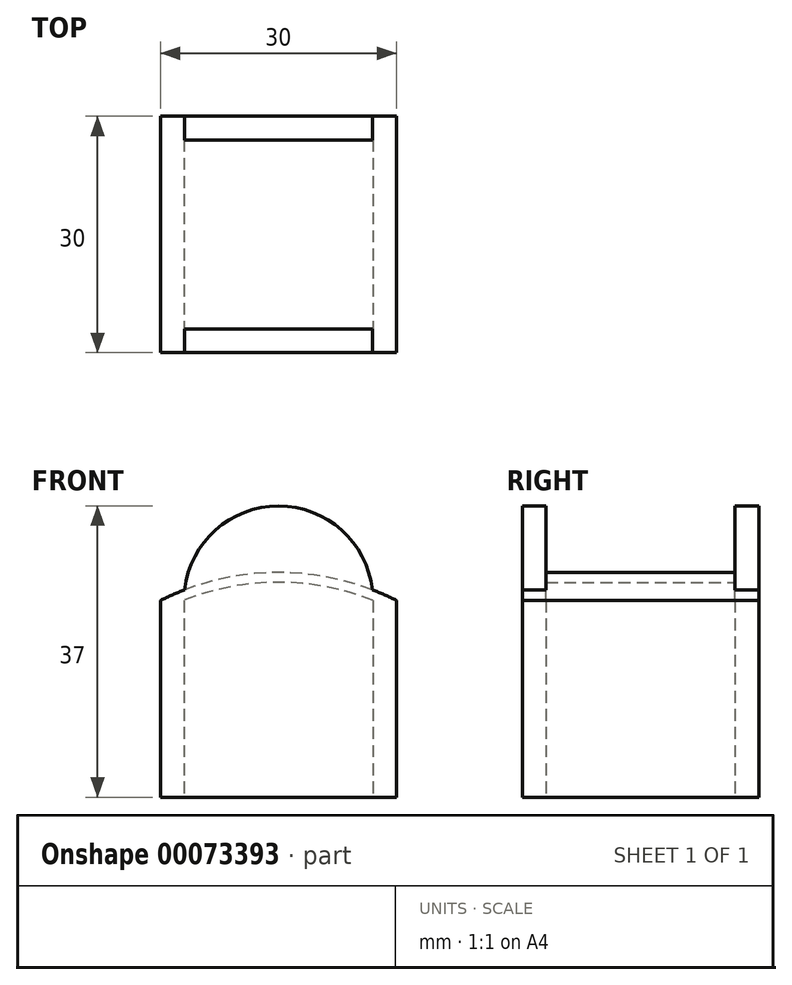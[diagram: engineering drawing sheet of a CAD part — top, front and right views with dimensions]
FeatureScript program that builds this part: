
annotation { "Feature Type Name" : "Feature", "Feature Type Description" : "" }
export const myFeature = defineFeature(function(context is Context, id is Id, definition is map)
    precondition{}
    {
        {
            var Q0;
            Q0=qCreatedBy(makeId("Top.planeOp"),FACE);
            var sketch = newSketch(context, id + "F0", { "sketchPlane" : qUnion([Q0])});
            skLineSegment(sketch, "E0.rect.bottom", {"start": v(15, 15) * mm, "end": v(-15, 15) * mm});
            skLineSegment(sketch, "E0.rect.top", {"start": v(15, -15) * mm, "end": v(-15, -15) * mm});
            skLineSegment(sketch, "E0.rect.left", {"start": v(15, 15) * mm, "end": v(15, -15) * mm});
            skLineSegment(sketch, "E0.rect.right", {"start": v(-15, 15) * mm, "end": v(-15, -15) * mm});
            skPoint(sketch, "E0.rect.middle", {"position": v(0, 0) * mm});
            skLineSegment(sketch, "E1.0", {"start": v(12, 12) * mm, "end": v(-12, 12) * mm});
            skLineSegment(sketch, "E1.1", {"start": v(12, 12) * mm, "end": v(12, -12) * mm});
            skLineSegment(sketch, "E1.2", {"start": v(12, -12) * mm, "end": v(-12, -12) * mm});
            skLineSegment(sketch, "E1.3", {"start": v(-12, 12) * mm, "end": v(-12, -12) * mm});
            skSolve(sketch);
        }
        {
            var Q0;
            Q0 = qSketchRegion(id + "F0", true);
            extrude(context, id + "F1", {"entities" : qUnion([Q0]), "depth" : 25 * mm});
        }
        {
            var Q0;
            Q0=qCreatedBy(makeId("Front.planeOp"),FACE);
            var sketch = newSketch(context, id + "F2", { "sketchPlane" : qUnion([Q0])});
            skArc(sketch, "E2", {"start": v(15, 25) * mm, "mid": v(0, 28.54) * mm, "end": v(-15, 25) * mm});
            skArc(sketch, "E3.0", {"start": v(12, 25) * mm, "mid": v(0, 27.31) * mm, "end": v(-12, 25) * mm});
            skLineSegment(sketch, "E4", {"start": v(-15, 25) * mm, "end": v(-12, 25) * mm});
            skLineSegment(sketch, "E5", {"start": v(12, 25) * mm, "end": v(15, 25) * mm});
            skLineSegment(sketch, "E6", {"start": v(0, 25) * mm, "end": v(0, -5) * mm, "construction": true});
            skLineSegment(sketch, "E7", {"start": v(-12, 25) * mm, "end": v(12, 25) * mm, "construction": true});
            skSolve(sketch);
        }
        {
            var Q0;
            Q0=makeQuery(id+"F2.imprint","IMPRINT",FACE,{"disambiguationData":[TD([[makeQuery(id+"F2.imprint","IMPRINT",EDGE,{"derivedFrom":sQuery(id+"F2.wireOp",EDGE,"E2")}),1.0]])]});
            var Q1;
            Q1=makeQuery(id+"F1.opExtrude","SWEPT_FACE",FACE,{"disambiguationData":[OSD([sQuery(id+"F0.wireOp",EDGE,"E0.rect.top")])]});
            var Q2;
            Q2=makeQuery(id+"F1.opExtrude","SWEPT_FACE",FACE,{"disambiguationData":[OSD([sQuery(id+"F0.wireOp",EDGE,"E0.rect.bottom")])]});
            extrude(context, id + "F3", {"entities" : qUnion([Q0]), "operationType" : NewBodyOperationType.ADD, "endBound" : BoundingType.UP_TO_SURFACE, "endBoundEntityFace" : qUnion([Q1]), "depth" : 25 * mm, "hasSecondDirection" : true, "secondDirectionBound" : SecondDirectionBoundingType.UP_TO_SURFACE, "secondDirectionOppositeDirection" : true, "secondDirectionBoundEntityFace" : qUnion([Q2]), "secondDirectionDepth" : 25 * mm});
        }
        {
            var Q0;
            Q0=makeQuery(id+"F3.boolean.opBoolean","MERGE",FACE,{"derivedFrom":[makeQuery(id+"F1.opExtrude","SWEPT_FACE",FACE,{"disambiguationData":[OSD([sQuery(id+"F0.wireOp",EDGE,"E0.rect.bottom")])]}),makeQuery(id+"F3.opExtrude","CAP_FACE",FACE,{"disambiguationData":[OSD([sQuery(id+"F2.wireOp",EDGE,"E2"),sQuery(id+"F2.wireOp",EDGE,"E3.0"),sQuery(id+"F2.wireOp",EDGE,"E4"),sQuery(id+"F2.wireOp",EDGE,"E5")])],"isStart":true})]});
            var sketch = newSketch(context, id + "F4", { "sketchPlane" : qUnion([Q0])});
            skArc(sketch, "E8", {"start": v(12, 25) * mm, "mid": v(0, 37) * mm, "end": v(-12, 25) * mm});
            skLineSegment(sketch, "E9", {"start": v(-12, 25) * mm, "end": v(12, 25) * mm});
            skSolve(sketch);
        }
        {
            var Q0;
            Q0 = qSketchRegion(id + "F4", true);
            var Q1;
            Q1=makeQuery(id+"F1.opExtrude","SWEPT_FACE",FACE,{"disambiguationData":[OSD([sQuery(id+"F0.wireOp",EDGE,"E1.0")])]});
            extrude(context, id + "F5", {"entities" : qUnion([Q0]), "operationType" : NewBodyOperationType.ADD, "endBound" : BoundingType.UP_TO_SURFACE, "oppositeDirection" : true, "endBoundEntityFace" : qUnion([Q1]), "depth" : 25 * mm});
        }
        {
            var Q0;
            Q0=makeQuery(id+"F3.boolean.opBoolean","MERGE",FACE,{"derivedFrom":[makeQuery(id+"F1.opExtrude","SWEPT_FACE",FACE,{"disambiguationData":[OSD([sQuery(id+"F0.wireOp",EDGE,"E0.rect.top")])]}),makeQuery(id+"F3.opExtrude","CAP_FACE",FACE,{"disambiguationData":[OSD([sQuery(id+"F2.wireOp",EDGE,"E2"),sQuery(id+"F2.wireOp",EDGE,"E3.0"),sQuery(id+"F2.wireOp",EDGE,"E4"),sQuery(id+"F2.wireOp",EDGE,"E5")])],"isStart":false})]});
            var sketch = newSketch(context, id + "F6", { "sketchPlane" : qUnion([Q0])});
            skArc(sketch, "E10", {"start": v(12, 25) * mm, "mid": v(0, 37) * mm, "end": v(-12, 25) * mm});
            skLineSegment(sketch, "E11", {"start": v(-12, 25) * mm, "end": v(12, 25) * mm});
            skSolve(sketch);
        }
        {
            var Q0;
            Q0 = qSketchRegion(id + "F6", true);
            var Q1;
            Q1=makeQuery(id+"F1.opExtrude","SWEPT_FACE",FACE,{"disambiguationData":[OSD([sQuery(id+"F0.wireOp",EDGE,"E1.2")])]});
            extrude(context, id + "F7", {"entities" : qUnion([Q0]), "operationType" : NewBodyOperationType.ADD, "endBound" : BoundingType.UP_TO_SURFACE, "oppositeDirection" : true, "endBoundEntityFace" : qUnion([Q1]), "depth" : 25 * mm});
        }
    });
